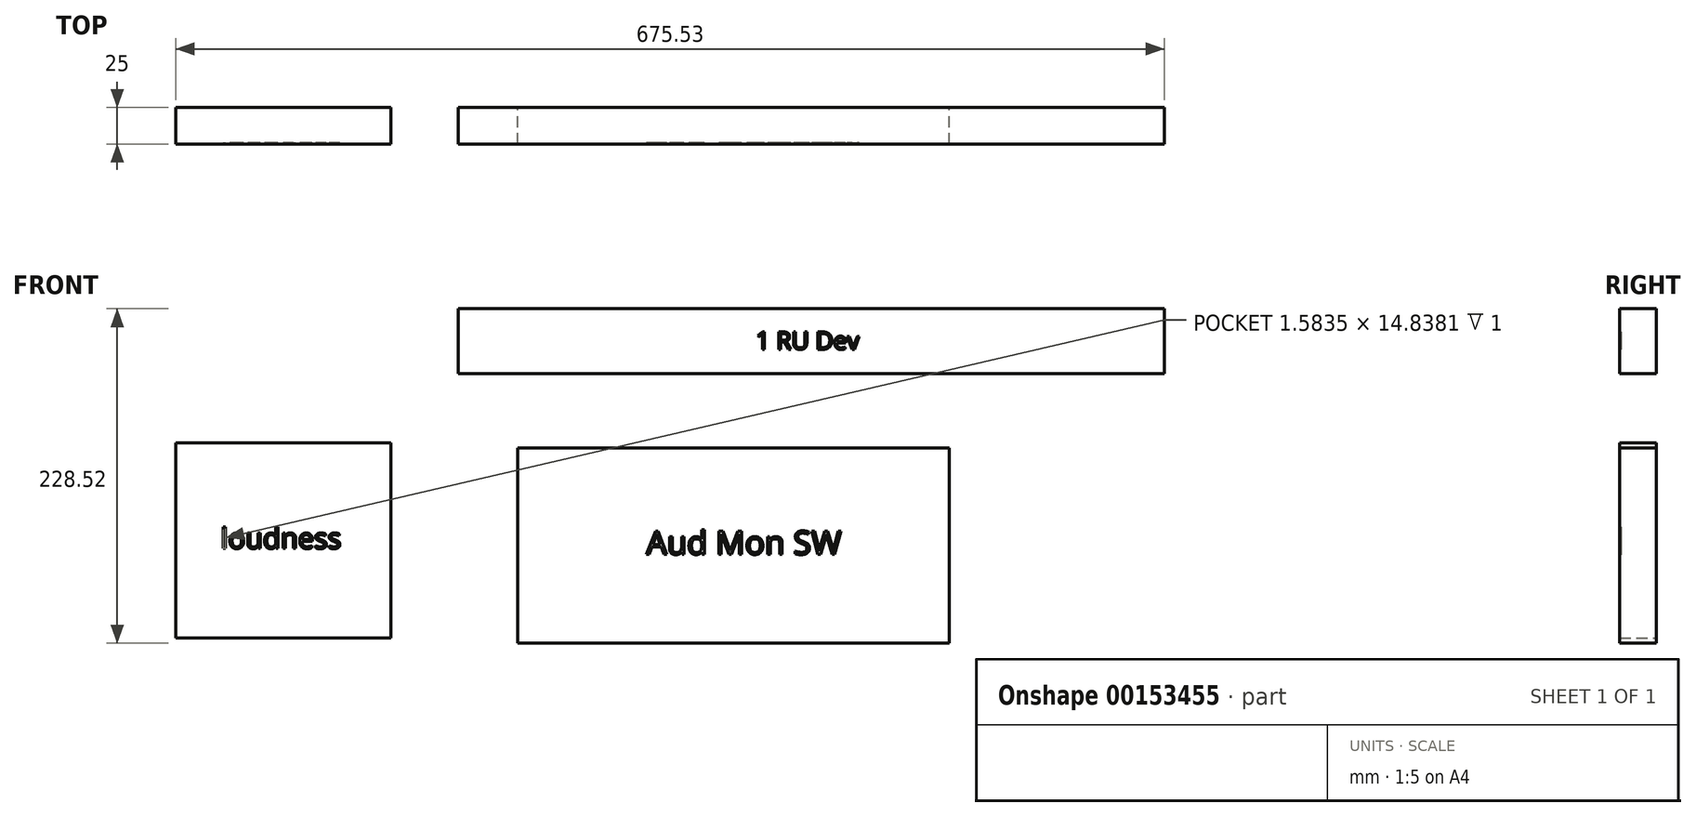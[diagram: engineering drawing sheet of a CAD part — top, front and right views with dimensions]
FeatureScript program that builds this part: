
annotation { "Feature Type Name" : "Feature", "Feature Type Description" : "" }
export const myFeature = defineFeature(function(context is Context, id is Id, definition is map)
    precondition{}
    {
        {
            var Q0;
            Q0=qCreatedBy(makeId("Front.planeOp"),FACE);
            var sketch = newSketch(context, id + "F0", { "sketchPlane" : qUnion([Q0])});
            skLineSegment(sketch, "E0.bottom", {"start": v(-494.72, 91.73) * mm, "end": v(-12.12, 91.73) * mm});
            skLineSegment(sketch, "E0.top", {"start": v(-494.72, 47.28) * mm, "end": v(-12.12, 47.28) * mm});
            skLineSegment(sketch, "E0.left", {"start": v(-494.72, 91.73) * mm, "end": v(-494.72, 47.28) * mm});
            skLineSegment(sketch, "E0.right", {"start": v(-12.12, 91.73) * mm, "end": v(-12.12, 47.28) * mm});
            skLineSegment(sketch, "E1.bottom", {"start": v(-687.65, 0) * mm, "end": v(-540.65, 0) * mm});
            skLineSegment(sketch, "E1.top", {"start": v(-687.65, -133.35) * mm, "end": v(-540.65, -133.35) * mm});
            skLineSegment(sketch, "E1.left", {"start": v(-687.65, 0) * mm, "end": v(-687.65, -133.35) * mm});
            skLineSegment(sketch, "E1.right", {"start": v(-540.65, 0) * mm, "end": v(-540.65, -133.35) * mm});
            skLineSegment(sketch, "E2.bottom", {"start": v(-454.09, -3.44) * mm, "end": v(-159.09, -3.44) * mm});
            skLineSegment(sketch, "E2.top", {"start": v(-454.09, -136.8) * mm, "end": v(-159.09, -136.8) * mm});
            skLineSegment(sketch, "E2.left", {"start": v(-454.09, -3.44) * mm, "end": v(-454.09, -136.8) * mm});
            skLineSegment(sketch, "E2.right", {"start": v(-159.09, -3.44) * mm, "end": v(-159.09, -136.8) * mm});
            skText(sketch, "E3", { "text": "1 RU Dev", "fontName": "OpenSans-Regular.ttf"});
            skText(sketch, "E4", { "text": "loudness", "fontName": "OpenSans-Regular.ttf"});
            skText(sketch, "E5", { "text": "Aud Mon SW", "fontName": "OpenSans-Regular.ttf"});
            const initialGuessF0  = {"E3": [-0.29131, 0.06391, 1, 0, 0.01205], "E4": [-0.65686, -0.07216, 1, 0, 0.01406], "E5": [-0.36613, -0.07618, 1, 0, 0.01607]};
            skSetInitialGuess(sketch, initialGuessF0);
            skSolve(sketch);
        }
        {
            var Q0;
            Q0=makeQuery(id+"F0.imprint","IMPRINT",FACE,{"disambiguationData":[TD([[makeQuery(id+"F0.imprint","IMPRINT",EDGE,{"derivedFrom":sQuery(id+"F0.wireOp",EDGE,"E0.bottom")}),-1.0]])]});
            var Q1;
            Q1=makeQuery(id+"F0.imprint","IMPRINT",FACE,{"disambiguationData":[TD([[makeQuery(id+"F0.imprint","IMPRINT",EDGE,{"derivedFrom":sQuery(id+"F0.wireOp",EDGE,"E3.sketch_text.stroke-0")}),-1.0]])]});
            var Q2;
            Q2=makeQuery(id+"F0.imprint","IMPRINT",FACE,{"disambiguationData":[TD([[makeQuery(id+"F0.imprint","IMPRINT",EDGE,{"derivedFrom":sQuery(id+"F0.wireOp",EDGE,"E3.sketch_text.stroke-9")}),-1.0]])]});
            var Q3;
            Q3=makeQuery(id+"F0.imprint","IMPRINT",FACE,{"disambiguationData":[TD([[makeQuery(id+"F0.imprint","IMPRINT",EDGE,{"derivedFrom":sQuery(id+"F0.wireOp",EDGE,"E3.sketch_text.stroke-20")}),1.0]])]});
            var Q4;
            Q4=makeQuery(id+"F0.imprint","IMPRINT",FACE,{"disambiguationData":[TD([[makeQuery(id+"F0.imprint","IMPRINT",EDGE,{"derivedFrom":sQuery(id+"F0.wireOp",EDGE,"E3.sketch_text.stroke-27")}),-1.0]])]});
            var Q5;
            Q5=makeQuery(id+"F0.imprint","IMPRINT",FACE,{"disambiguationData":[TD([[makeQuery(id+"F0.imprint","IMPRINT",EDGE,{"derivedFrom":sQuery(id+"F0.wireOp",EDGE,"E3.sketch_text.stroke-48")}),1.0]])]});
            var Q6;
            Q6=makeQuery(id+"F0.imprint","IMPRINT",FACE,{"disambiguationData":[TD([[makeQuery(id+"F0.imprint","IMPRINT",EDGE,{"derivedFrom":sQuery(id+"F0.wireOp",EDGE,"E3.sketch_text.stroke-41")}),-1.0]])]});
            var Q7;
            Q7=makeQuery(id+"F0.imprint","IMPRINT",FACE,{"disambiguationData":[TD([[makeQuery(id+"F0.imprint","IMPRINT",EDGE,{"derivedFrom":sQuery(id+"F0.wireOp",EDGE,"E3.sketch_text.stroke-69")}),1.0]])]});
            var Q8;
            Q8=makeQuery(id+"F0.imprint","IMPRINT",FACE,{"disambiguationData":[TD([[makeQuery(id+"F0.imprint","IMPRINT",EDGE,{"derivedFrom":sQuery(id+"F0.wireOp",EDGE,"E3.sketch_text.stroke-55")}),-1.0]])]});
            var Q9;
            Q9=makeQuery(id+"F0.imprint","IMPRINT",FACE,{"disambiguationData":[TD([[makeQuery(id+"F0.imprint","IMPRINT",EDGE,{"derivedFrom":sQuery(id+"F0.wireOp",EDGE,"E3.sketch_text.stroke-74")}),-1.0]])]});
            extrude(context, id + "F1", {"entities" : qUnion([Q0, Q1, Q2, Q3, Q4, Q5, Q6, Q7, Q8, Q9]), "depth" : 24 * mm});
        }
        {
            var Q0;
            Q0=makeQuery(id+"F0.imprint","IMPRINT",FACE,{"disambiguationData":[TD([[makeQuery(id+"F0.imprint","IMPRINT",EDGE,{"derivedFrom":sQuery(id+"F0.wireOp",EDGE,"E4.sketch_text.stroke-21")}),-1.0]])]});
            var Q1;
            Q1=makeQuery(id+"F0.imprint","IMPRINT",FACE,{"disambiguationData":[TD([[makeQuery(id+"F0.imprint","IMPRINT",EDGE,{"derivedFrom":sQuery(id+"F0.wireOp",EDGE,"E4.sketch_text.stroke-38")}),-1.0]])]});
            var Q2;
            Q2=makeQuery(id+"F0.imprint","IMPRINT",FACE,{"disambiguationData":[TD([[makeQuery(id+"F0.imprint","IMPRINT",EDGE,{"derivedFrom":sQuery(id+"F0.wireOp",EDGE,"E4.sketch_text.stroke-62")}),-1.0]])]});
            var Q3;
            Q3=makeQuery(id+"F0.imprint","IMPRINT",FACE,{"disambiguationData":[TD([[makeQuery(id+"F0.imprint","IMPRINT",EDGE,{"derivedFrom":sQuery(id+"F0.wireOp",EDGE,"E4.sketch_text.stroke-79")}),-1.0]])]});
            var Q4;
            Q4=makeQuery(id+"F0.imprint","IMPRINT",FACE,{"disambiguationData":[TD([[makeQuery(id+"F0.imprint","IMPRINT",EDGE,{"derivedFrom":sQuery(id+"F0.wireOp",EDGE,"E4.sketch_text.stroke-98")}),-1.0]])]});
            var Q5;
            Q5=makeQuery(id+"F0.imprint","IMPRINT",FACE,{"disambiguationData":[TD([[makeQuery(id+"F0.imprint","IMPRINT",EDGE,{"derivedFrom":sQuery(id+"F0.wireOp",EDGE,"E4.sketch_text.stroke-123")}),-1.0]])]});
            var Q6;
            Q6=makeQuery(id+"F0.imprint","IMPRINT",FACE,{"disambiguationData":[TD([[makeQuery(id+"F0.imprint","IMPRINT",EDGE,{"derivedFrom":sQuery(id+"F0.wireOp",EDGE,"E4.sketch_text.stroke-4")}),-1.0]])]});
            var Q7;
            Q7=makeQuery(id+"F0.imprint","IMPRINT",FACE,{"disambiguationData":[TD([[makeQuery(id+"F0.imprint","IMPRINT",EDGE,{"derivedFrom":sQuery(id+"F0.wireOp",EDGE,"E4.sketch_text.stroke-0")}),-1.0]])]});
            var Q8;
            Q8=makeQuery(id+"F0.imprint","IMPRINT",FACE,{"disambiguationData":[TD([[makeQuery(id+"F0.imprint","IMPRINT",EDGE,{"derivedFrom":sQuery(id+"F0.wireOp",EDGE,"E4.sketch_text.stroke-13")}),1.0]])]});
            var Q9;
            Q9=makeQuery(id+"F0.imprint","IMPRINT",FACE,{"disambiguationData":[TD([[makeQuery(id+"F0.imprint","IMPRINT",EDGE,{"derivedFrom":sQuery(id+"F0.wireOp",EDGE,"E4.sketch_text.stroke-53")}),1.0]])]});
            var Q10;
            Q10=makeQuery(id+"F0.imprint","IMPRINT",FACE,{"disambiguationData":[TD([[makeQuery(id+"F0.imprint","IMPRINT",EDGE,{"derivedFrom":sQuery(id+"F0.wireOp",EDGE,"E4.sketch_text.stroke-93")}),1.0]])]});
            var Q11;
            Q11=makeQuery(id+"F0.imprint","IMPRINT",FACE,{"disambiguationData":[TD([[makeQuery(id+"F0.imprint","IMPRINT",EDGE,{"derivedFrom":sQuery(id+"F0.wireOp",EDGE,"E1.bottom")}),-1.0]])]});
            extrude(context, id + "F2", {"entities" : qUnion([Q0, Q1, Q2, Q3, Q4, Q5, Q6, Q7, Q8, Q9, Q10, Q11]), "depth" : 24 * mm});
        }
        {
            var Q0;
            Q0=makeQuery(id+"F0.imprint","IMPRINT",FACE,{"disambiguationData":[TD([[makeQuery(id+"F0.imprint","IMPRINT",EDGE,{"derivedFrom":sQuery(id+"F0.wireOp",EDGE,"E1.bottom")}),-1.0]])]});
            var Q1;
            Q1=makeQuery(id+"F0.imprint","IMPRINT",FACE,{"disambiguationData":[TD([[makeQuery(id+"F0.imprint","IMPRINT",EDGE,{"derivedFrom":sQuery(id+"F0.wireOp",EDGE,"E4.sketch_text.stroke-13")}),1.0]])]});
            var Q2;
            Q2=makeQuery(id+"F0.imprint","IMPRINT",FACE,{"disambiguationData":[TD([[makeQuery(id+"F0.imprint","IMPRINT",EDGE,{"derivedFrom":sQuery(id+"F0.wireOp",EDGE,"E4.sketch_text.stroke-53")}),1.0]])]});
            var Q3;
            Q3=makeQuery(id+"F0.imprint","IMPRINT",FACE,{"disambiguationData":[TD([[makeQuery(id+"F0.imprint","IMPRINT",EDGE,{"derivedFrom":sQuery(id+"F0.wireOp",EDGE,"E4.sketch_text.stroke-93")}),1.0]])]});
            extrude(context, id + "F3", {"entities" : qUnion([Q0, Q1, Q2, Q3]), "operationType" : NewBodyOperationType.ADD, "depth" : 25 * mm});
        }
        {
            var Q0;
            Q0=makeQuery(id+"F0.imprint","IMPRINT",FACE,{"disambiguationData":[TD([[makeQuery(id+"F0.imprint","IMPRINT",EDGE,{"derivedFrom":sQuery(id+"F0.wireOp",EDGE,"E2.bottom")}),-1.0]])]});
            var Q1;
            Q1=makeQuery(id+"F0.imprint","IMPRINT",FACE,{"disambiguationData":[TD([[makeQuery(id+"F0.imprint","IMPRINT",EDGE,{"derivedFrom":sQuery(id+"F0.wireOp",EDGE,"E5.sketch_text.stroke-45")}),1.0]])]});
            var Q2;
            Q2=makeQuery(id+"F0.imprint","IMPRINT",FACE,{"disambiguationData":[TD([[makeQuery(id+"F0.imprint","IMPRINT",EDGE,{"derivedFrom":sQuery(id+"F0.wireOp",EDGE,"E5.sketch_text.stroke-8")}),1.0]])]});
            var Q3;
            Q3=makeQuery(id+"F0.imprint","IMPRINT",FACE,{"disambiguationData":[TD([[makeQuery(id+"F0.imprint","IMPRINT",EDGE,{"derivedFrom":sQuery(id+"F0.wireOp",EDGE,"E5.sketch_text.stroke-81")}),1.0]])]});
            var Q4;
            Q4=makeQuery(id+"F0.imprint","IMPRINT",FACE,{"disambiguationData":[TD([[makeQuery(id+"F0.imprint","IMPRINT",EDGE,{"derivedFrom":sQuery(id+"F0.wireOp",EDGE,"E5.sketch_text.stroke-0")}),-1.0]])]});
            var Q5;
            Q5=makeQuery(id+"F0.imprint","IMPRINT",FACE,{"disambiguationData":[TD([[makeQuery(id+"F0.imprint","IMPRINT",EDGE,{"derivedFrom":sQuery(id+"F0.wireOp",EDGE,"E5.sketch_text.stroke-13")}),-1.0]])]});
            var Q6;
            Q6=makeQuery(id+"F0.imprint","IMPRINT",FACE,{"disambiguationData":[TD([[makeQuery(id+"F0.imprint","IMPRINT",EDGE,{"derivedFrom":sQuery(id+"F0.wireOp",EDGE,"E5.sketch_text.stroke-30")}),-1.0]])]});
            var Q7;
            Q7=makeQuery(id+"F0.imprint","IMPRINT",FACE,{"disambiguationData":[TD([[makeQuery(id+"F0.imprint","IMPRINT",EDGE,{"derivedFrom":sQuery(id+"F0.wireOp",EDGE,"E5.sketch_text.stroke-54")}),-1.0]])]});
            var Q8;
            Q8=makeQuery(id+"F0.imprint","IMPRINT",FACE,{"disambiguationData":[TD([[makeQuery(id+"F0.imprint","IMPRINT",EDGE,{"derivedFrom":sQuery(id+"F0.wireOp",EDGE,"E5.sketch_text.stroke-72")}),-1.0]])]});
            var Q9;
            Q9=makeQuery(id+"F0.imprint","IMPRINT",FACE,{"disambiguationData":[TD([[makeQuery(id+"F0.imprint","IMPRINT",EDGE,{"derivedFrom":sQuery(id+"F0.wireOp",EDGE,"E5.sketch_text.stroke-89")}),-1.0]])]});
            var Q10;
            Q10=makeQuery(id+"F0.imprint","IMPRINT",FACE,{"disambiguationData":[TD([[makeQuery(id+"F0.imprint","IMPRINT",EDGE,{"derivedFrom":sQuery(id+"F0.wireOp",EDGE,"E5.sketch_text.stroke-106")}),-1.0]])]});
            var Q11;
            Q11=makeQuery(id+"F0.imprint","IMPRINT",FACE,{"disambiguationData":[TD([[makeQuery(id+"F0.imprint","IMPRINT",EDGE,{"derivedFrom":sQuery(id+"F0.wireOp",EDGE,"E5.sketch_text.stroke-131")}),-1.0]])]});
            extrude(context, id + "F4", {"entities" : qUnion([Q0, Q1, Q2, Q3, Q4, Q5, Q6, Q7, Q8, Q9, Q10, Q11]), "depth" : 24 * mm});
        }
        {
            var Q0;
            Q0=makeQuery(id+"F0.imprint","IMPRINT",FACE,{"disambiguationData":[TD([[makeQuery(id+"F0.imprint","IMPRINT",EDGE,{"derivedFrom":sQuery(id+"F0.wireOp",EDGE,"E5.sketch_text.stroke-45")}),1.0]])]});
            var Q1;
            Q1=makeQuery(id+"F0.imprint","IMPRINT",FACE,{"disambiguationData":[TD([[makeQuery(id+"F0.imprint","IMPRINT",EDGE,{"derivedFrom":sQuery(id+"F0.wireOp",EDGE,"E5.sketch_text.stroke-81")}),1.0]])]});
            var Q2;
            Q2=makeQuery(id+"F0.imprint","IMPRINT",FACE,{"disambiguationData":[TD([[makeQuery(id+"F0.imprint","IMPRINT",EDGE,{"derivedFrom":sQuery(id+"F0.wireOp",EDGE,"E5.sketch_text.stroke-8")}),1.0]])]});
            var Q3;
            Q3=makeQuery(id+"F0.imprint","IMPRINT",FACE,{"disambiguationData":[TD([[makeQuery(id+"F0.imprint","IMPRINT",EDGE,{"derivedFrom":sQuery(id+"F0.wireOp",EDGE,"E2.bottom")}),-1.0]])]});
            extrude(context, id + "F5", {"entities" : qUnion([Q0, Q1, Q2, Q3]), "operationType" : NewBodyOperationType.ADD, "depth" : 25 * mm});
        }
        {
            var Q0;
            Q0=makeQuery(id+"F0.imprint","IMPRINT",FACE,{"disambiguationData":[TD([[makeQuery(id+"F0.imprint","IMPRINT",EDGE,{"derivedFrom":sQuery(id+"F0.wireOp",EDGE,"E3.sketch_text.stroke-20")}),1.0]])]});
            var Q1;
            Q1=makeQuery(id+"F0.imprint","IMPRINT",FACE,{"disambiguationData":[TD([[makeQuery(id+"F0.imprint","IMPRINT",EDGE,{"derivedFrom":sQuery(id+"F0.wireOp",EDGE,"E0.bottom")}),-1.0]])]});
            var Q2;
            Q2=makeQuery(id+"F0.imprint","IMPRINT",FACE,{"disambiguationData":[TD([[makeQuery(id+"F0.imprint","IMPRINT",EDGE,{"derivedFrom":sQuery(id+"F0.wireOp",EDGE,"E3.sketch_text.stroke-48")}),1.0]])]});
            var Q3;
            Q3=makeQuery(id+"F0.imprint","IMPRINT",FACE,{"disambiguationData":[TD([[makeQuery(id+"F0.imprint","IMPRINT",EDGE,{"derivedFrom":sQuery(id+"F0.wireOp",EDGE,"E3.sketch_text.stroke-69")}),1.0]])]});
            extrude(context, id + "F6", {"entities" : qUnion([Q0, Q1, Q2, Q3]), "operationType" : NewBodyOperationType.ADD, "depth" : 25 * mm});
        }
    });
